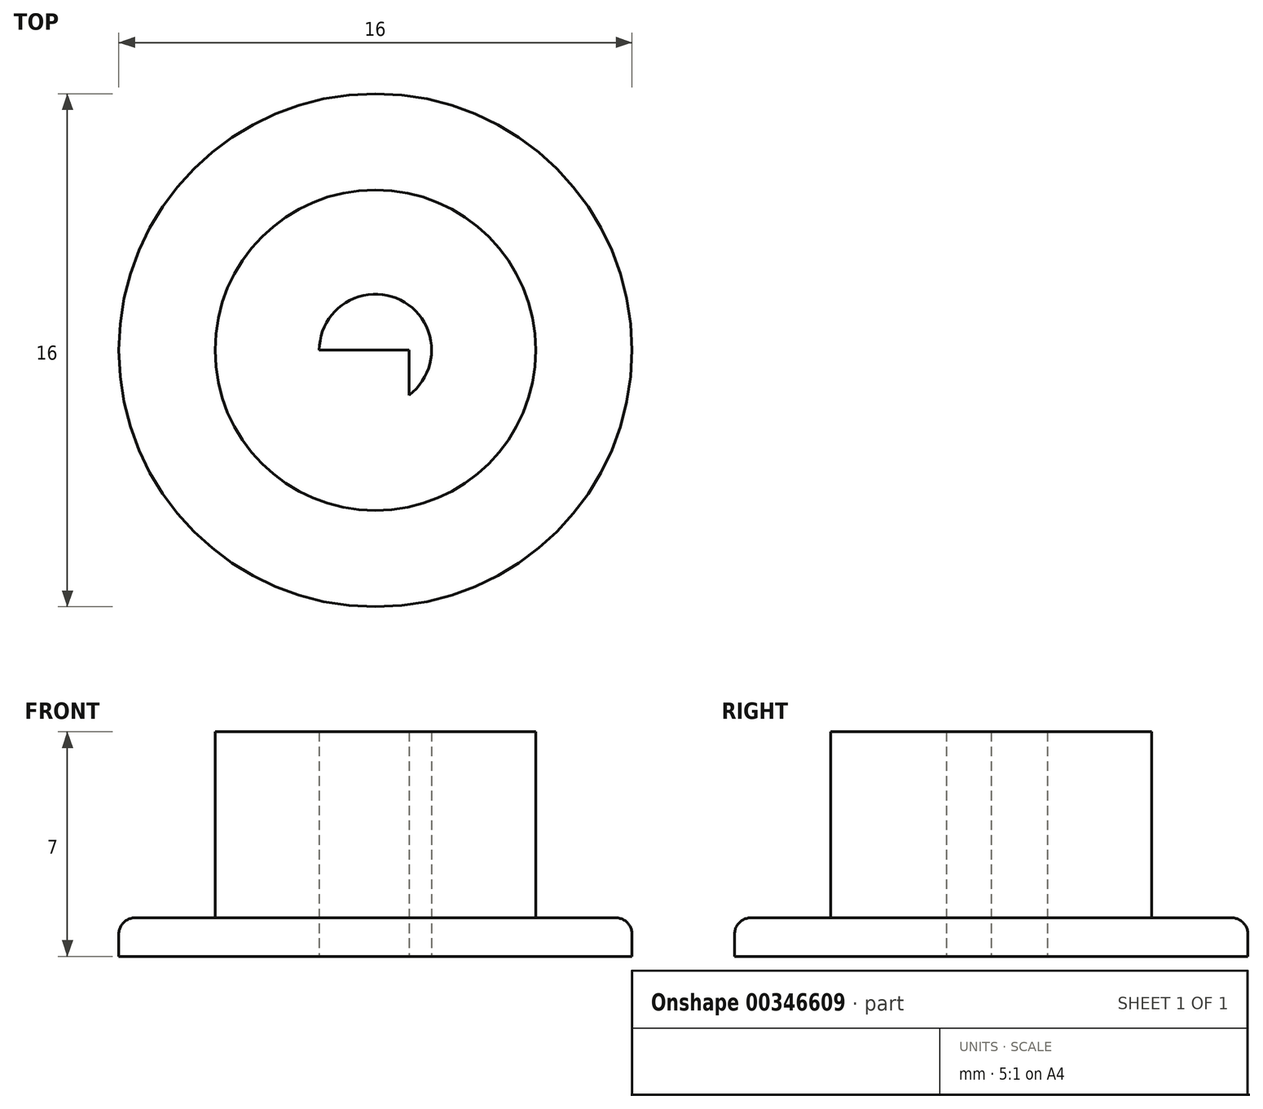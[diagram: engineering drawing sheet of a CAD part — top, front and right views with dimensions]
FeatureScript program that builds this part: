
annotation { "Feature Type Name" : "Feature", "Feature Type Description" : "" }
export const myFeature = defineFeature(function(context is Context, id is Id, definition is map)
    precondition{}
    {
        {
            var Q0;
            Q0=qCreatedBy(makeId("Top.planeOp"),FACE);
            var sketch = newSketch(context, id + "F0", { "sketchPlane" : qUnion([Q0])});
            skCircle(sketch, "E0", {"center": v(0, 0) * mm, "radius": 8 * mm});
            skCircle(sketch, "E1", {"center": v(0, 0) * mm, "radius": 5 * mm});
            skCircle(sketch, "E2", {"center": v(0, 0) * mm, "radius": 1.75 * mm});
            skLineSegment(sketch, "E3", {"start": v(-1.75, 0) * mm, "end": v(1.05, 0) * mm});
            skLineSegment(sketch, "E4", {"start": v(1.05, 0) * mm, "end": v(1.05, 1.4) * mm});
            skLineSegment(sketch, "E5", {"start": v(1.05, 1.4) * mm, "end": v(1.05, -1.4) * mm});
            skSolve(sketch);
        }
        {
            var Q0;
            Q0=makeQuery(id+"F0.imprint","IMPRINT",FACE,{"disambiguationData":[TD([[makeQuery(id+"F0.imprint","IMPRINT",EDGE,{"derivedFrom":sQuery(id+"F0.wireOp",EDGE,"E1")}),1.0]])]});
            var Q1;
            {var subQ0=sQuery(id+"F0.wireOp",EDGE,"E5");var subQ1=sQuery(id+"F0.wireOp",EDGE,"E2");var subQ2=makeQuery(id+"F0.imprint","INTERSECT",VERTEX,{"disambiguationData":[OD(0.0)],"derivedFrom":[subQ1,subQ0]});Q1=makeQuery(id+"F0.imprint","IMPRINT",FACE,{"disambiguationData":[TD([[makeQuery(id+"F0.imprint","IMPRINT",EDGE,{"disambiguationData":[TD([[subQ2,1.0]])],"derivedFrom":subQ1}),1.0]])]});}
            extrude(context, id + "F1", {"entities" : qUnion([Q0, Q1]), "depth" : 7 * mm});
        }
        {
            var Q0;
            Q0=makeQuery(id+"F0.imprint","IMPRINT",FACE,{"disambiguationData":[TD([[makeQuery(id+"F0.imprint","IMPRINT",EDGE,{"derivedFrom":sQuery(id+"F0.wireOp",EDGE,"E0")}),1.0]])]});
            extrude(context, id + "F2", {"entities" : qUnion([Q0]), "operationType" : NewBodyOperationType.ADD, "depth" : 1.2 * mm});
        }
        {
            var Q0;
            Q0=makeQuery(id+"F2.opExtrude","CAP_EDGE",EDGE,{"disambiguationData":[OSD([sQuery(id+"F0.wireOp",EDGE,"E0")])],"isStart":false});
            fillet(context, id + "F3", {"entities" : qUnion([Q0]), "radius" : 0.5 * mm, "tangentPropagation" : true, "allowEdgeOverflow" : false});
        }
    });
